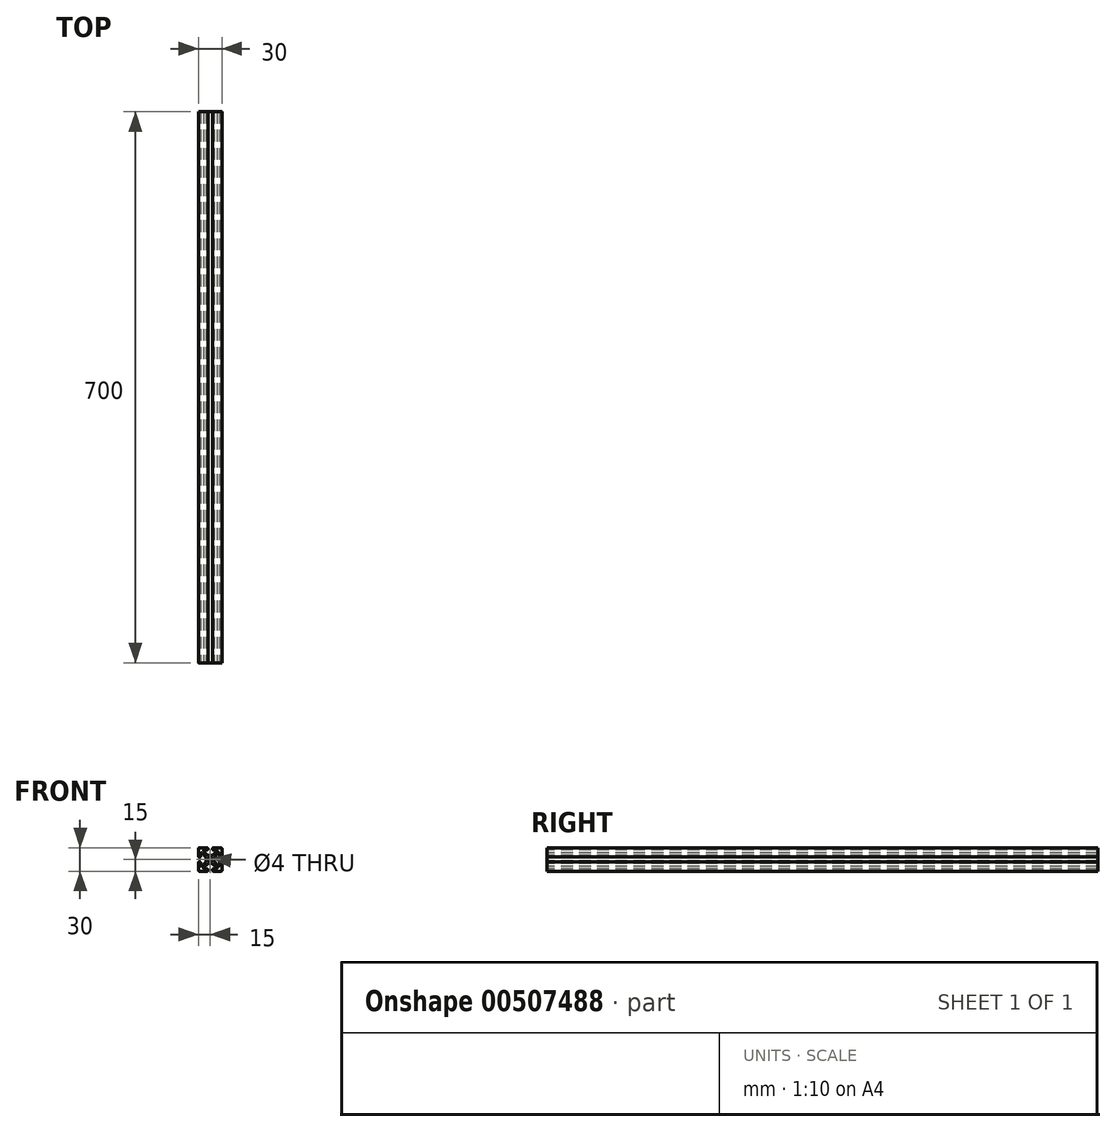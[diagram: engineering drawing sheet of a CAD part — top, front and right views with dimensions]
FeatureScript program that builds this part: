
annotation { "Feature Type Name" : "Feature", "Feature Type Description" : "" }
export const myFeature = defineFeature(function(context is Context, id is Id, definition is map)
    precondition{}
    {
        {
            var Q0;
            Q0=qCreatedBy(makeId("Front.planeOp"),FACE);
            var sketch = newSketch(context, id + "F0", { "sketchPlane" : qUnion([Q0])});
            skLineSegment(sketch, "E0.bottom", {"start": v(13.5, 15) * mm, "end": v(4, 15) * mm});
            skLineSegment(sketch, "E0.top", {"start": v(13.5, -15) * mm, "end": v(4, -15) * mm});
            skLineSegment(sketch, "E0.left", {"start": v(15, 13.5) * mm, "end": v(15, 4) * mm});
            skLineSegment(sketch, "E0.right", {"start": v(-15, 13.5) * mm, "end": v(-15, 4) * mm});
            skPoint(sketch, "E0.middle", {"position": v(0, 0) * mm});
            skLineSegment(sketch, "E1.bottom", {"start": v(7.46, 12) * mm, "end": v(4, 12) * mm});
            skLineSegment(sketch, "E1.top", {"start": v(7.46, -12) * mm, "end": v(4, -12) * mm});
            skLineSegment(sketch, "E1.left", {"start": v(12, 7.46) * mm, "end": v(12, 4) * mm});
            skLineSegment(sketch, "E1.right", {"start": v(-12, 7.46) * mm, "end": v(-12, 4) * mm});
            skLineSegment(sketch, "E2", {"start": v(8.17, 10.3) * mm, "end": v(3.32, 5.44) * mm});
            skLineSegment(sketch, "E3", {"start": v(-8.17, -10.3) * mm, "end": v(-3.32, -5.44) * mm});
            skLineSegment(sketch, "E4", {"start": v(-8.17, 10.3) * mm, "end": v(-3.32, 5.44) * mm});
            skLineSegment(sketch, "E5", {"start": v(-10.3, 8.17) * mm, "end": v(-5, 2.88) * mm});
            skPoint(sketch, "E6.orphan", {"position": v(12, 12) * mm});
            skPoint(sketch, "E7.orphan", {"position": v(12, -12) * mm});
            skPoint(sketch, "E8.orphan", {"position": v(-12, -12) * mm});
            skPoint(sketch, "E9.orphan", {"position": v(-12, 12) * mm});
            skLineSegment(sketch, "E10.trimOffspring", {"start": v(-5.44, -3.32) * mm, "end": v(-10.3, -8.17) * mm});
            skLineSegment(sketch, "E11.trimOffspring", {"start": v(5.44, -3.32) * mm, "end": v(10.3, -8.17) * mm});
            skLineSegment(sketch, "E12.trimOffspring", {"start": v(5.44, 3.32) * mm, "end": v(10.3, 8.17) * mm});
            skLineSegment(sketch, "E13.trimOffspring", {"start": v(3.32, -5.44) * mm, "end": v(8.17, -10.3) * mm});
            skLineSegment(sketch, "E14.bottom", {"start": v(2.26, 5) * mm, "end": v(-2.26, 5) * mm});
            skLineSegment(sketch, "E14.top", {"start": v(2.26, -5) * mm, "end": v(-2.26, -5) * mm});
            skLineSegment(sketch, "E14.left", {"start": v(5, 2.26) * mm, "end": v(5, -2.26) * mm});
            skLineSegment(sketch, "E14.right", {"start": v(-5, 2.88) * mm, "end": v(-5, -2.26) * mm});
            skPoint(sketch, "E15.orphan", {"position": v(5, 5) * mm});
            skPoint(sketch, "E16.orphan", {"position": v(5, -5) * mm});
            skPoint(sketch, "E17.orphan", {"position": v(-5, -5) * mm});
            skPoint(sketch, "E18.orphan", {"position": v(-5, 5) * mm});
            skCircle(sketch, "E19", {"center": v(0, 0) * mm, "radius": 2 * mm});
            skLineSegment(sketch, "E20", {"start": v(-3, 14) * mm, "end": v(-3, 13) * mm});
            skLineSegment(sketch, "E21", {"start": v(3, 14) * mm, "end": v(3, 13) * mm});
            skLineSegment(sketch, "E22.trimOffspring", {"start": v(-3, -13) * mm, "end": v(-3, -14) * mm});
            skLineSegment(sketch, "E23.trimOffspring", {"start": v(-4, 12) * mm, "end": v(-7.46, 12) * mm});
            skLineSegment(sketch, "E24.trimOffspring", {"start": v(-4, 15) * mm, "end": v(-13.5, 15) * mm});
            skLineSegment(sketch, "E25.trimOffspring", {"start": v(3, -13) * mm, "end": v(3, -14) * mm});
            skLineSegment(sketch, "E26.trimOffspring", {"start": v(-4, -12) * mm, "end": v(-7.46, -12) * mm});
            skLineSegment(sketch, "E27.trimOffspring", {"start": v(-4, -15) * mm, "end": v(-13.5, -15) * mm});
            skLineSegment(sketch, "E28", {"start": v(-14, 3) * mm, "end": v(-13, 3) * mm});
            skLineSegment(sketch, "E29", {"start": v(-14, -3) * mm, "end": v(-13, -3) * mm});
            skLineSegment(sketch, "E30.trimOffspring", {"start": v(-12, -4) * mm, "end": v(-12, -7.46) * mm});
            skLineSegment(sketch, "E31.trimOffspring", {"start": v(-15, -4) * mm, "end": v(-15, -13.5) * mm});
            skLineSegment(sketch, "E32.trimOffspring", {"start": v(13, 3) * mm, "end": v(14, 3) * mm});
            skLineSegment(sketch, "E33.trimOffspring", {"start": v(13, -3) * mm, "end": v(14, -3) * mm});
            skLineSegment(sketch, "E34.trimOffspring", {"start": v(12, -4) * mm, "end": v(12, -7.46) * mm});
            skLineSegment(sketch, "E35.trimOffspring", {"start": v(15, -4) * mm, "end": v(15, -13.5) * mm});
            skPoint(sketch, "E36.visualSharp", {"position": v(-15, 15) * mm});
            skArc(sketch, "E36.filletArc", {"start": v(-13.5, 15) * mm, "mid": v(-14.56, 14.56) * mm, "end": v(-15, 13.5) * mm});
            skPoint(sketch, "E37.visualSharp", {"position": v(15, 15) * mm});
            skArc(sketch, "E37.filletArc", {"start": v(15, 13.5) * mm, "mid": v(14.56, 14.56) * mm, "end": v(13.5, 15) * mm});
            skPoint(sketch, "E38.visualSharp", {"position": v(15, -15) * mm});
            skArc(sketch, "E38.filletArc", {"start": v(13.5, -15) * mm, "mid": v(14.56, -14.56) * mm, "end": v(15, -13.5) * mm});
            skPoint(sketch, "E39.visualSharp", {"position": v(-15, -15) * mm});
            skArc(sketch, "E39.filletArc", {"start": v(-15, -13.5) * mm, "mid": v(-14.56, -14.56) * mm, "end": v(-13.5, -15) * mm});
            skPoint(sketch, "E40.visualSharp", {"position": v(-5, -2.88) * mm});
            skArc(sketch, "E40.filletArc", {"start": v(-5.44, -3.32) * mm, "mid": v(-5.11, -2.83) * mm, "end": v(-5, -2.26) * mm});
            skPoint(sketch, "E41.visualSharp", {"position": v(-2.88, -5) * mm});
            skArc(sketch, "E41.filletArc", {"start": v(-2.26, -5) * mm, "mid": v(-2.83, -5.11) * mm, "end": v(-3.32, -5.44) * mm});
            skPoint(sketch, "E42.visualSharp", {"position": v(2.88, -5) * mm});
            skArc(sketch, "E42.filletArc", {"start": v(3.32, -5.44) * mm, "mid": v(2.83, -5.11) * mm, "end": v(2.26, -5) * mm});
            skPoint(sketch, "E43.visualSharp", {"position": v(5, -2.88) * mm});
            skArc(sketch, "E43.filletArc", {"start": v(5, -2.26) * mm, "mid": v(5.11, -2.83) * mm, "end": v(5.44, -3.32) * mm});
            skPoint(sketch, "E44.visualSharp", {"position": v(5, 2.88) * mm});
            skArc(sketch, "E44.filletArc", {"start": v(5.44, 3.32) * mm, "mid": v(5.11, 2.83) * mm, "end": v(5, 2.26) * mm});
            skPoint(sketch, "E45.visualSharp", {"position": v(2.88, 5) * mm});
            skArc(sketch, "E45.filletArc", {"start": v(2.26, 5) * mm, "mid": v(2.83, 5.11) * mm, "end": v(3.32, 5.44) * mm});
            skPoint(sketch, "E46.visualSharp", {"position": v(-2.88, 5) * mm});
            skArc(sketch, "E46.filletArc", {"start": v(-3.32, 5.44) * mm, "mid": v(-2.83, 5.11) * mm, "end": v(-2.26, 5) * mm});
            skPoint(sketch, "E47.visualSharp", {"position": v(-3, 12) * mm});
            skArc(sketch, "E47.filletArc", {"start": v(-4, 12) * mm, "mid": v(-3.3, 12.3) * mm, "end": v(-3, 13) * mm});
            skPoint(sketch, "E48.visualSharp", {"position": v(-3, 15) * mm});
            skArc(sketch, "E48.filletArc", {"start": v(-3, 14) * mm, "mid": v(-3.3, 14.7) * mm, "end": v(-4, 15) * mm});
            skPoint(sketch, "E49.visualSharp", {"position": v(3, 15) * mm});
            skArc(sketch, "E49.filletArc", {"start": v(4, 15) * mm, "mid": v(3.3, 14.7) * mm, "end": v(3, 14) * mm});
            skPoint(sketch, "E50.visualSharp", {"position": v(3, 12) * mm});
            skArc(sketch, "E50.filletArc", {"start": v(3, 13) * mm, "mid": v(3.3, 12.3) * mm, "end": v(4, 12) * mm});
            skPoint(sketch, "E51.visualSharp", {"position": v(12, 3) * mm});
            skArc(sketch, "E51.filletArc", {"start": v(12, 4) * mm, "mid": v(12.3, 3.3) * mm, "end": v(13, 3) * mm});
            skPoint(sketch, "E52.visualSharp", {"position": v(15, 3) * mm});
            skArc(sketch, "E52.filletArc", {"start": v(14, 3) * mm, "mid": v(14.7, 3.3) * mm, "end": v(15, 4) * mm});
            skPoint(sketch, "E53.visualSharp", {"position": v(15, -3) * mm});
            skArc(sketch, "E53.filletArc", {"start": v(15, -4) * mm, "mid": v(14.7, -3.3) * mm, "end": v(14, -3) * mm});
            skPoint(sketch, "E54.visualSharp", {"position": v(12, -3) * mm});
            skArc(sketch, "E54.filletArc", {"start": v(13, -3) * mm, "mid": v(12.3, -3.3) * mm, "end": v(12, -4) * mm});
            skPoint(sketch, "E55.visualSharp", {"position": v(3, -12) * mm});
            skArc(sketch, "E55.filletArc", {"start": v(4, -12) * mm, "mid": v(3.3, -12.3) * mm, "end": v(3, -13) * mm});
            skPoint(sketch, "E56.visualSharp", {"position": v(3, -15) * mm});
            skArc(sketch, "E56.filletArc", {"start": v(3, -14) * mm, "mid": v(3.3, -14.7) * mm, "end": v(4, -15) * mm});
            skPoint(sketch, "E57.visualSharp", {"position": v(-3, -12) * mm});
            skArc(sketch, "E57.filletArc", {"start": v(-3, -13) * mm, "mid": v(-3.3, -12.3) * mm, "end": v(-4, -12) * mm});
            skPoint(sketch, "E58.visualSharp", {"position": v(-3, -15) * mm});
            skArc(sketch, "E58.filletArc", {"start": v(-4, -15) * mm, "mid": v(-3.3, -14.7) * mm, "end": v(-3, -14) * mm});
            skPoint(sketch, "E59.visualSharp", {"position": v(-12, -3) * mm});
            skArc(sketch, "E59.filletArc", {"start": v(-12, -4) * mm, "mid": v(-12.3, -3.3) * mm, "end": v(-13, -3) * mm});
            skPoint(sketch, "E60.visualSharp", {"position": v(-15, -3) * mm});
            skArc(sketch, "E60.filletArc", {"start": v(-14, -3) * mm, "mid": v(-14.7, -3.3) * mm, "end": v(-15, -4) * mm});
            skPoint(sketch, "E61.visualSharp", {"position": v(-15, 3) * mm});
            skArc(sketch, "E61.filletArc", {"start": v(-15, 4) * mm, "mid": v(-14.7, 3.3) * mm, "end": v(-14, 3) * mm});
            skPoint(sketch, "E62.visualSharp", {"position": v(-12, 3) * mm});
            skArc(sketch, "E62.filletArc", {"start": v(-13, 3) * mm, "mid": v(-12.3, 3.3) * mm, "end": v(-12, 4) * mm});
            skPoint(sketch, "E63.visualSharp", {"position": v(9.88, 12) * mm});
            skArc(sketch, "E63.filletArc", {"start": v(8.17, 10.3) * mm, "mid": v(8.39, 11.38) * mm, "end": v(7.46, 12) * mm});
            skPoint(sketch, "E64.visualSharp", {"position": v(12, 9.88) * mm});
            skArc(sketch, "E64.filletArc", {"start": v(12, 7.46) * mm, "mid": v(11.38, 8.39) * mm, "end": v(10.3, 8.17) * mm});
            skPoint(sketch, "E65.visualSharp", {"position": v(12, -9.88) * mm});
            skArc(sketch, "E65.filletArc", {"start": v(10.3, -8.17) * mm, "mid": v(11.38, -8.39) * mm, "end": v(12, -7.46) * mm});
            skPoint(sketch, "E66.visualSharp", {"position": v(9.88, -12) * mm});
            skArc(sketch, "E66.filletArc", {"start": v(7.46, -12) * mm, "mid": v(8.39, -11.38) * mm, "end": v(8.17, -10.3) * mm});
            skPoint(sketch, "E67.visualSharp", {"position": v(-12, -9.88) * mm});
            skArc(sketch, "E67.filletArc", {"start": v(-12, -7.46) * mm, "mid": v(-11.38, -8.39) * mm, "end": v(-10.3, -8.17) * mm});
            skPoint(sketch, "E68.visualSharp", {"position": v(-9.88, -12) * mm});
            skArc(sketch, "E68.filletArc", {"start": v(-8.17, -10.3) * mm, "mid": v(-8.39, -11.38) * mm, "end": v(-7.46, -12) * mm});
            skPoint(sketch, "E69.visualSharp", {"position": v(-12, 9.88) * mm});
            skArc(sketch, "E69.filletArc", {"start": v(-10.3, 8.17) * mm, "mid": v(-11.38, 8.39) * mm, "end": v(-12, 7.46) * mm});
            skPoint(sketch, "E70.visualSharp", {"position": v(-9.88, 12) * mm});
            skArc(sketch, "E70.filletArc", {"start": v(-7.46, 12) * mm, "mid": v(-8.39, 11.38) * mm, "end": v(-8.17, 10.3) * mm});
            skSolve(sketch);
        }
        {
            var Q0;
            Q0=qSketchRegion(id+"F0",true);
            extrude(context, id + "F1", {"entities" : qUnion([Q0]), "oppositeDirection" : true, "depth" : 700 * mm});
        }
    });
